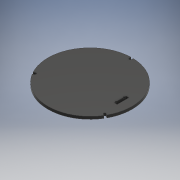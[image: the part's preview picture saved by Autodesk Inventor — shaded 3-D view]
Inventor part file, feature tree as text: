
AUTODESK INVENTOR PART (.ipt)
format: ipt  version: 2017 (Build 210142000, 142)  size: 203,776 bytes
history: native  units: mm
features: extrude x6, sketch x6, projected_geometry x3, fillet x2
ambient origin geometry x8: Origin, YZ Plane, XZ Plane, XY Plane, X Axis, Y Axis, Z Axis, Center Point
bodies: Solid1 (feature_tree)
feature tree (17):
  extrude  "Extrusion1"  Depth=2.0mm TaperAngle=0.0deg
  extrude  "Extrusion2"  Depth=1.8mm
  extrude  "Extrusion3"  Depth=2.0mm TaperAngle=0.0deg
  extrude  "Extrusion4"  Depth=9.0mm
  extrude  "Extrusion5"  Depth=3.0mm
  extrude  "Extrusion6"  Depth=1.0mm
  fillet  "Fillet1"  Radius=1.0mm
  fillet  "Fillet2"  Radius=1.0mm
  sketch  "Sketch1"  dims[d0=64.0mm d1=2.0mm d2=0.0mm]
  sketch  "Sketch2"  dims[d3=30.658mm d4=1.8mm]
  projected_geometry  "Projected Loop1"
  sketch  "Sketch3"  dims[d5=30.0mm d7=360.0deg d9=2.0mm d10=0.0mm]
  sketch  "Sketch4"  dims[d11=2.2mm d12=9.0mm]
  projected_geometry  "Projected Loop2"
  sketch  "Sketch5"  dims[d13=2.0mm d14=0.0mm d15=3.0mm]
  projected_geometry  "Projected Loop3"
  sketch  "Sketch6"  dims[d16=3.0mm d17=1.0mm d18=1.0mm d19=1.0mm d20=0.0mm d21=57.63mm d22=24.0mm d23=2.0mm d24=57.63mm d25=2.0mm d26=0.0mm d27=15.5mm d28=2.0mm d29=8.5mm d30=8.5mm d31=2.0mm d32=16.0mm d33=0.0mm d34=2.0mm d35=2.0mm]
